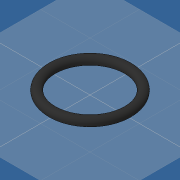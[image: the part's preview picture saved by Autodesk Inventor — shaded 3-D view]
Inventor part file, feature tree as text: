
AUTODESK INVENTOR PART (.ipt)
format: ipt  version: 2019 (Build 230136000, 136)  size: 111,104 bytes
history: native  units: mm
features: revolve x1, sketch x1
ambient origin geometry x8: Origin, YZ Plane, XZ Plane, XY Plane, X Axis, Y Axis, Z Axis, Center Point
bodies: Volumenkörper1 (feature_tree)
feature tree (2):
  revolve  "Umdrehung1"
  sketch  "Skizze1"  dims[d1=3.5mm d2=34.0mm d3=90.0deg]
